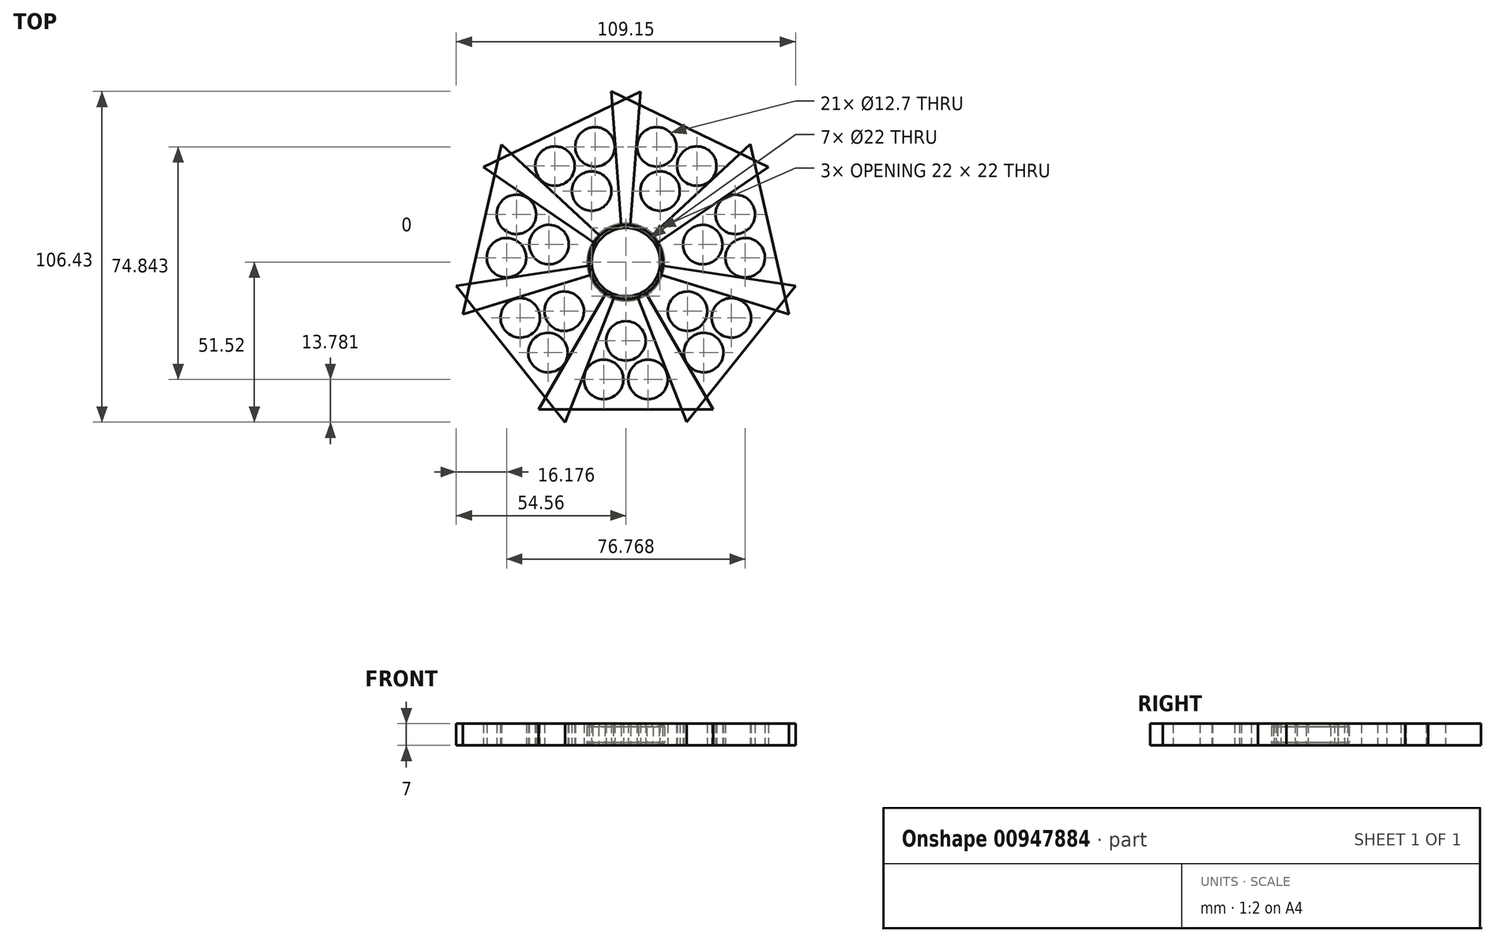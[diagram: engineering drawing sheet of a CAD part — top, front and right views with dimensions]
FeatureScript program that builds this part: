
annotation { "Feature Type Name" : "Feature", "Feature Type Description" : "" }
export const myFeature = defineFeature(function(context is Context, id is Id, definition is map)
    precondition{}
    {
        {
            var Q0;
            Q0=qCreatedBy(makeId("Top.planeOp"),FACE);
            var sketch = newSketch(context, id + "F0", { "sketchPlane" : qUnion([Q0])});
            skCircle(sketch, "E0", {"center": v(0, 0) * mm, "radius": 12.5 * mm});
            skSolve(sketch);
        }
        {
            var Q0;
            Q0=qSketchRegion(id+"F0",true);
            extrude(context, id + "F1", {"entities" : qUnion([Q0]), "depth" : 7 * mm, "offsetDistance" : 25.4 * mm});
        }
        {
            var Q0;
            Q0=qCreatedBy(makeId("Top.planeOp"),FACE);
            var sketch = newSketch(context, id + "F2", { "sketchPlane" : qUnion([Q0])});
            skCircle(sketch, "E1.cCircle", {"center": v(0.03, -31.23) * mm, "radius": 16.2 * mm, "construction": true});
            skLineSegment(sketch, "E1.0", {"start": v(28.08, -47.42) * mm, "end": v(-28.03, -47.42) * mm});
            skLineSegment(sketch, "E1.1", {"start": v(-28.03, -47.42) * mm, "end": v(0.03, 1.17) * mm});
            skLineSegment(sketch, "E1.2", {"start": v(0.03, 1.17) * mm, "end": v(28.08, -47.42) * mm});
            skPoint(sketch, "E1.0.midPoint", {"position": v(0.03, -47.42) * mm});
            skSolve(sketch);
        }
        {
            var Q0;
            Q0=qSketchRegion(id+"F2",true);
            var Q1;
            Q1=qSketchRegion(id+"F0",true);
            extrude(context, id + "F3", {"entities" : qUnion([Q0, Q1]), "operationType" : NewBodyOperationType.ADD, "depth" : 7 * mm, "offsetDistance" : 25.4 * mm});
        }
        {
            var Q0;
            Q0=makeQuery(id+"F3.opExtrude","CAP_EDGE",EDGE,{"disambiguationData":[OSD([sQuery(id+"F2.wireOp",EDGE,"kZWvsPfk-VZJj-Ojfw-RwgL-EVQD4XRQKU4n.left")])],"isStart":false});
            var Q1;
            Q1=makeQuery(id+"F3.opExtrude","CAP_EDGE",EDGE,{"disambiguationData":[OSD([sQuery(id+"F2.wireOp",EDGE,"kZWvsPfk-VZJj-Ojfw-RwgL-EVQD4XRQKU4n.right")])],"isStart":false});
            var Q2;
            Q2=makeQuery(id+"F1.opExtrude","CAP_EDGE",EDGE,{"disambiguationData":[OSD([sQuery(id+"F0.wireOp",EDGE,"E0")])],"isStart":false});
            chamfer(context, id + "F4", {"entities" : qUnion([Q0, Q1, Q2]), "chamferType" : ChamferType.OFFSET_ANGLE, "width" : 1 * mm, "oppositeDirection" : true, "angle" : 30 * degree, "tangentPropagation" : true});
        }
        {
            var Q0;
            Q0=makeQuery(id+"F3.opExtrude","CAP_EDGE",EDGE,{"disambiguationData":[OSD([sQuery(id+"F2.wireOp",EDGE,"kZWvsPfk-VZJj-Ojfw-RwgL-EVQD4XRQKU4n.left")])],"isStart":true});
            var Q1;
            Q1=makeQuery(id+"F3.opExtrude","CAP_EDGE",EDGE,{"disambiguationData":[OSD([sQuery(id+"F2.wireOp",EDGE,"kZWvsPfk-VZJj-Ojfw-RwgL-EVQD4XRQKU4n.right")])],"isStart":true});
            var Q2;
            Q2=makeQuery(id+"F1.opExtrude","CAP_EDGE",EDGE,{"disambiguationData":[OSD([sQuery(id+"F0.wireOp",EDGE,"E0")])],"isStart":true});
            chamfer(context, id + "F5", {"entities" : qUnion([Q0, Q1, Q2]), "chamferType" : ChamferType.OFFSET_ANGLE, "width" : 1 * mm, "oppositeDirection" : false, "angle" : 30 * degree, "tangentPropagation" : true});
        }
        {
            var Q0;
            Q0=qCreatedBy(makeId("Top.planeOp"),FACE);
            var sketch = newSketch(context, id + "F6", { "sketchPlane" : qUnion([Q0])});
            skCircle(sketch, "E2.cCircle", {"center": v(0, -33.61) * mm, "radius": 4.13 * mm, "construction": true});
            skLineSegment(sketch, "E2.0", {"start": v(7.15, -37.74) * mm, "end": v(-7.15, -37.74) * mm});
            skLineSegment(sketch, "E2.1", {"start": v(-7.15, -37.74) * mm, "end": v(0, -25.36) * mm});
            skLineSegment(sketch, "E2.2", {"start": v(0, -25.36) * mm, "end": v(7.15, -37.74) * mm});
            skPoint(sketch, "E2.0.midPoint", {"position": v(0, -37.74) * mm});
            skSolve(sketch);
        }
        {
            var Q0;
            Q0=sQuery(id+"F6.wireOp",VERTEX,"E2.1.end");
            var Q1;
            Q1=sQuery(id+"F6.wireOp",VERTEX,"E2.0.start");
            var Q2;
            Q2=sQuery(id+"F6.wireOp",VERTEX,"E2.0.end");
            var Q3;
            Q3=makeQuery(id+"F1.opExtrude","SWEPT_BODY",BODY,{"disambiguationData":[OSD([sQuery(id+"F0.wireOp",EDGE,"E0")])]});
            hole(context, id + "F7", {"style" : HoleStyle.SIMPLE, "endStyle" : HoleEndStyle.THROUGH, "oppositeDirection" : true, "holeDiameter" : 12.7 * mm, "majorDiameter" : 6.35 * mm, "isTappedThrough" : true, "tappedDepth" : 12.7 * mm, "tapClearance" : 3, "locations" : qUnion([Q0, Q1, Q2]), "scope" : qUnion([Q3])});
        }
        {
            var Q0;
            Q0=makeQuery(id+"F1.opExtrude","SWEPT_BODY",BODY,{"disambiguationData":[OSD([sQuery(id+"F0.wireOp",EDGE,"E0")])]});
            var Q1;
            Q1=makeQuery(id+"F1.opExtrude","SWEPT_FACE",FACE,{"disambiguationData":[OSD([sQuery(id+"F0.wireOp",EDGE,"E0")])]});
            circularPattern(context, id + "F8", {"entities" : qUnion([Q0]), "axis" : qUnion([Q1]), "angle" : 360 * degree, "instanceCount" : 7, "equalSpace" : true});
        }
        {
            var Q0;
            Q0=qCreatedBy(makeId("Top.planeOp"),FACE);
            var sketch = newSketch(context, id + "F9", { "sketchPlane" : qUnion([Q0])});
            skPoint(sketch, "E3", {"position": v(0, 0) * mm});
            skSolve(sketch);
        }
        {
            var Q0;
            Q0=sQuery(id+"F9.wireOp",VERTEX,"E3");
            var Q1;
            Q1=makeQuery(id+"F1.opExtrude","SWEPT_BODY",BODY,{"disambiguationData":[OSD([sQuery(id+"F0.wireOp",EDGE,"E0")])]});
            var Q2;
            Q2=makeQuery(id+"F8.opPattern","COPY",BODY,{"derivedFrom":makeQuery(id+"F1.opExtrude","SWEPT_BODY",BODY,{"disambiguationData":[OSD([sQuery(id+"F0.wireOp",EDGE,"E0")])]}),"instanceName":"1"});
            var Q3;
            Q3=makeQuery(id+"F8.opPattern","COPY",BODY,{"derivedFrom":makeQuery(id+"F1.opExtrude","SWEPT_BODY",BODY,{"disambiguationData":[OSD([sQuery(id+"F0.wireOp",EDGE,"E0")])]}),"instanceName":"2"});
            var Q4;
            Q4=makeQuery(id+"F8.opPattern","COPY",BODY,{"derivedFrom":makeQuery(id+"F1.opExtrude","SWEPT_BODY",BODY,{"disambiguationData":[OSD([sQuery(id+"F0.wireOp",EDGE,"E0")])]}),"instanceName":"3"});
            var Q5;
            Q5=makeQuery(id+"F8.opPattern","COPY",BODY,{"derivedFrom":makeQuery(id+"F1.opExtrude","SWEPT_BODY",BODY,{"disambiguationData":[OSD([sQuery(id+"F0.wireOp",EDGE,"E0")])]}),"instanceName":"4"});
            var Q6;
            Q6=makeQuery(id+"F8.opPattern","COPY",BODY,{"derivedFrom":makeQuery(id+"F1.opExtrude","SWEPT_BODY",BODY,{"disambiguationData":[OSD([sQuery(id+"F0.wireOp",EDGE,"E0")])]}),"instanceName":"5"});
            var Q7;
            Q7=makeQuery(id+"F8.opPattern","COPY",BODY,{"derivedFrom":makeQuery(id+"F1.opExtrude","SWEPT_BODY",BODY,{"disambiguationData":[OSD([sQuery(id+"F0.wireOp",EDGE,"E0")])]}),"instanceName":"6"});
            hole(context, id + "F10", {"style" : HoleStyle.SIMPLE, "endStyle" : HoleEndStyle.THROUGH, "oppositeDirection" : true, "holeDiameter" : 22 * mm, "majorDiameter" : 5 * mm, "isTappedThrough" : true, "tappedDepth" : 12.7 * mm, "tapClearance" : 3, "locations" : qUnion([Q0]), "scope" : qUnion([Q1, Q2, Q3, Q4, Q5, Q6, Q7])});
        }
    });
